# Revit family: Gira_267730
name_source: partatom
category: Electrical Fixtures
revit_build: Autodesk Revit 2017 (Build: 20160225_1515(x64)
units: mm (PartAtom-declared; Revit-internal decimal feet)

## family parameters
Cut with Voids When Loaded = No
Host = Face
Maintain Annotation Orientation = Yes
Part Type = Normal
Room Calculation Point = No
Round Connector Dimension = Use Diameter
Shared = No

## types (1)
- RCD-prot.sock. 30 mA HC + SH WP surface-mounted p.white
    Available = No
    BIM (1) = https://media.stage.bim.site
    Category = Socket outlet
    Data sheet (1) = https://katalog.gira.de
    Default Elevation = 1219 mm
    Description = RCD-prot.sock.30mA SH WP SM PW,RCD-protected socket outlet 30 mA with hinged cover, integrated increased contact protection (shutter) and symbol ,,pure white,Features:,- The RCD-protected socket outlet is a permanently installed protective device with voltage-dependent residual current tripping in accordance with VDE0664.,- This device works like an RCD switch.,- Additional SCHUKO socket outlets can be connected to the connection wires, which are then also included in the residual current protection.,,Notes :,- Increased contact protection pursuant to DIN-VDE 0620-1.
    GTIN = 4010337028925
    HAN = 267730
    HeinzeBIM = https://bimportal.heinze.de
    Manufacturer = Gira
    Manufacturer URL = https://www.gira.de
    Model = Other
    Name = RCD-prot.sock. 30 mA HC + SH WP surface-mounted p.white
    Rated fault current = 0.03
    Transparent = No
    URL = http://katalog.gira.de

## geometry (parser evidence)
native form markers: Blend x2, Sweep x3
no freeform markers — native parametric forms only
